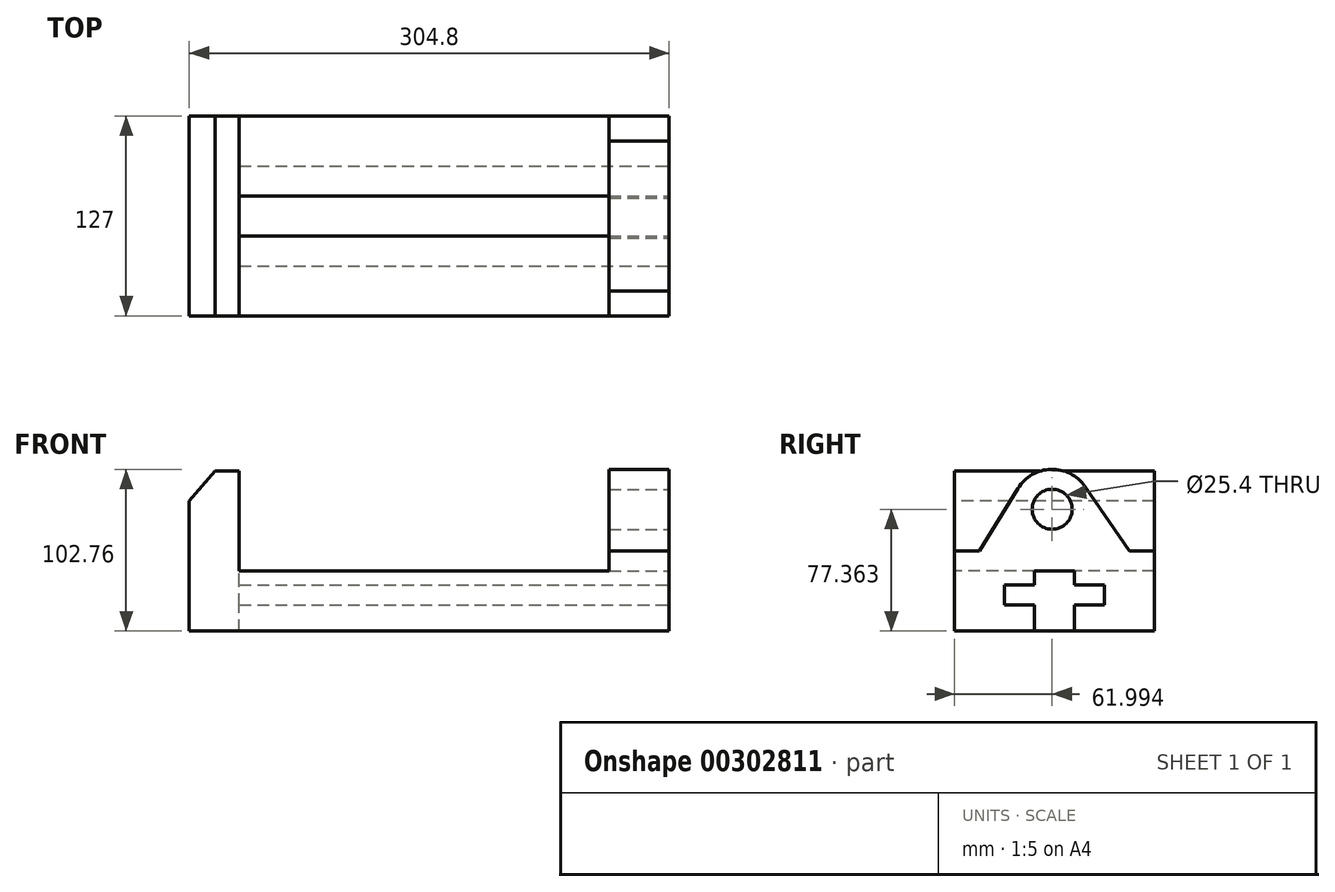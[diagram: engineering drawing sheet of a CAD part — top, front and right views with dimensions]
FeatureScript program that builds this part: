
annotation { "Feature Type Name" : "Feature", "Feature Type Description" : "" }
export const myFeature = defineFeature(function(context is Context, id is Id, definition is map)
    precondition{}
    {
        {
            var Q0;
            Q0=qCreatedBy(makeId("Front.planeOp"),FACE);
            var sketch = newSketch(context, id + "F0", { "sketchPlane" : qUnion([Q0])});
            skLineSegment(sketch, "E0", {"start": v(0, 0) * mm, "end": v(0, 38.1) * mm});
            skLineSegment(sketch, "E1", {"start": v(0, 38.1) * mm, "end": v(304.8, 38.1) * mm});
            skLineSegment(sketch, "E2", {"start": v(0, 0) * mm, "end": v(304.8, 0) * mm});
            skLineSegment(sketch, "E3", {"start": v(304.8, 0) * mm, "end": v(304.8, 38.1) * mm});
            skSolve(sketch);
        }
        {
            var Q0;
            Q0 = qSketchRegion(id + "F0", true);
            extrude(context, id + "F1", {"entities" : qUnion([Q0]), "endBound" : BoundingType.SYMMETRIC, "depth" : 127 * mm});
        }
        {
            var Q0;
            Q0=makeQuery(id+"F1.opExtrude","CAP_FACE",FACE,{"disambiguationData":[OSD([sQuery(id+"F0.wireOp",EDGE,"E0"),sQuery(id+"F0.wireOp",EDGE,"E1"),sQuery(id+"F0.wireOp",EDGE,"E2"),sQuery(id+"F0.wireOp",EDGE,"E3")])],"isStart":false});
            var sketch = newSketch(context, id + "F2", { "sketchPlane" : qUnion([Q0])});
            skLineSegment(sketch, "E4", {"start": v(0, 38.1) * mm, "end": v(31.75, 38.1) * mm});
            skLineSegment(sketch, "E5", {"start": v(31.75, 38.1) * mm, "end": v(31.75, 101.6) * mm});
            skLineSegment(sketch, "E6", {"start": v(0, 38.1) * mm, "end": v(0, 82.55) * mm});
            skLineSegment(sketch, "E7", {"start": v(31.75, 101.6) * mm, "end": v(16.5, 101.6) * mm});
            skLineSegment(sketch, "E8", {"start": v(16.5, 101.6) * mm, "end": v(0, 82.55) * mm});
            skSolve(sketch);
        }
        {
            var Q0;
            Q0 = qSketchRegion(id + "F2", true);
            extrude(context, id + "F3", {"entities" : qUnion([Q0]), "operationType" : NewBodyOperationType.ADD, "oppositeDirection" : true, "depth" : 127 * mm});
        }
        {
            var Q0;
            Q0=makeQuery(id+"F1.opExtrude","SWEPT_FACE",FACE,{"disambiguationData":[OSD([sQuery(id+"F0.wireOp",EDGE,"E3")])]});
            var sketch = newSketch(context, id + "F4", { "sketchPlane" : qUnion([Q0])});
            skLineSegment(sketch, "E9", {"start": v(-63.5, 0) * mm, "end": v(-63.5, 50.8) * mm});
            skLineSegment(sketch, "E10", {"start": v(-63.5, 0) * mm, "end": v(63.5, 0) * mm});
            skLineSegment(sketch, "E11", {"start": v(63.5, 0) * mm, "end": v(63.5, 50.8) * mm});
            skLineSegment(sketch, "E12", {"start": v(-63.5, 50.8) * mm, "end": v(-47.62, 50.8) * mm});
            skLineSegment(sketch, "E13", {"start": v(63.5, 50.8) * mm, "end": v(47.62, 50.8) * mm});
            skLineSegment(sketch, "E14", {"start": v(-47.62, 50.8) * mm, "end": v(-23.15, 90.65) * mm});
            skLineSegment(sketch, "E15", {"start": v(47.62, 50.8) * mm, "end": v(19.41, 91.77) * mm});
            skArc(sketch, "E16", {"start": v(19.41, 91.77) * mm, "mid": v(-2.17, 102.75) * mm, "end": v(-23.15, 90.65) * mm});
            skSolve(sketch);
        }
        {
            var Q0;
            Q0 = qSketchRegion(id + "F4", true);
            extrude(context, id + "F5", {"entities" : qUnion([Q0]), "operationType" : NewBodyOperationType.ADD, "oppositeDirection" : true, "depth" : 38.1 * mm});
        }
        {
            var Q0;
            Q0=makeQuery(id+"F5.boolean.opBoolean","MERGE",FACE,{"derivedFrom":[makeQuery(id+"F1.opExtrude","SWEPT_FACE",FACE,{"disambiguationData":[OSD([sQuery(id+"F0.wireOp",EDGE,"E3")])]}),makeQuery(id+"F5.opExtrude","CAP_FACE",FACE,{"disambiguationData":[OSD([sQuery(id+"F4.wireOp",EDGE,"E9"),sQuery(id+"F4.wireOp",EDGE,"E10"),sQuery(id+"F4.wireOp",EDGE,"E11"),sQuery(id+"F4.wireOp",EDGE,"E12"),sQuery(id+"F4.wireOp",EDGE,"E13"),sQuery(id+"F4.wireOp",EDGE,"E14"),sQuery(id+"F4.wireOp",EDGE,"E15"),sQuery(id+"F4.wireOp",EDGE,"E16")])],"isStart":true})]});
            var sketch = newSketch(context, id + "F6", { "sketchPlane" : qUnion([Q0])});
            skCircle(sketch, "E17", {"center": v(-1.5, 77.36) * mm, "radius": 12.7 * mm});
            skSolve(sketch);
        }
        {
            var Q0;
            Q0 = qSketchRegion(id + "F6", true);
            extrude(context, id + "F7", {"entities" : qUnion([Q0]), "operationType" : NewBodyOperationType.REMOVE, "oppositeDirection" : true, "depth" : 55.88 * mm});
        }
        {
            var Q0;
            Q0=makeQuery(id+"F5.boolean.opBoolean","MERGE",FACE,{"derivedFrom":[makeQuery(id+"F1.opExtrude","SWEPT_FACE",FACE,{"disambiguationData":[OSD([sQuery(id+"F0.wireOp",EDGE,"E3")])]}),makeQuery(id+"F5.opExtrude","CAP_FACE",FACE,{"disambiguationData":[OSD([sQuery(id+"F4.wireOp",EDGE,"E9"),sQuery(id+"F4.wireOp",EDGE,"E10"),sQuery(id+"F4.wireOp",EDGE,"E11"),sQuery(id+"F4.wireOp",EDGE,"E12"),sQuery(id+"F4.wireOp",EDGE,"E13"),sQuery(id+"F4.wireOp",EDGE,"E14"),sQuery(id+"F4.wireOp",EDGE,"E15"),sQuery(id+"F4.wireOp",EDGE,"E16")])],"isStart":true})]});
            var sketch = newSketch(context, id + "F8", { "sketchPlane" : qUnion([Q0])});
            skLineSegment(sketch, "E18", {"start": v(0, 0) * mm, "end": v(-12.7, 0) * mm});
            skLineSegment(sketch, "E19", {"start": v(0, 0) * mm, "end": v(12.7, 0) * mm});
            skLineSegment(sketch, "E20", {"start": v(-12.7, 0) * mm, "end": v(-12.7, 16.51) * mm});
            skLineSegment(sketch, "E21", {"start": v(-12.7, 16.51) * mm, "end": v(-31.75, 16.51) * mm});
            skLineSegment(sketch, "E22", {"start": v(-31.75, 16.51) * mm, "end": v(-31.75, 29.21) * mm});
            skLineSegment(sketch, "E23", {"start": v(-31.75, 29.21) * mm, "end": v(-12.7, 29.21) * mm});
            skLineSegment(sketch, "E24", {"start": v(-12.7, 29.21) * mm, "end": v(-12.7, 38.1) * mm});
            skLineSegment(sketch, "E25", {"start": v(-12.7, 38.1) * mm, "end": v(12.7, 38.1) * mm});
            skLineSegment(sketch, "E26", {"start": v(12.7, 38.1) * mm, "end": v(12.7, 29.21) * mm});
            skLineSegment(sketch, "E27", {"start": v(12.7, 29.21) * mm, "end": v(31.75, 29.21) * mm});
            skLineSegment(sketch, "E28", {"start": v(31.75, 29.21) * mm, "end": v(31.75, 16.51) * mm});
            skLineSegment(sketch, "E29", {"start": v(31.75, 16.51) * mm, "end": v(12.7, 16.51) * mm});
            skLineSegment(sketch, "E30", {"start": v(12.7, 16.51) * mm, "end": v(12.7, 0) * mm});
            skSolve(sketch);
        }
        {
            var Q0;
            Q0 = qSketchRegion(id + "F8", true);
            extrude(context, id + "F9", {"entities" : qUnion([Q0]), "operationType" : NewBodyOperationType.REMOVE, "oppositeDirection" : true, "depth" : 273.05 * mm});
        }
    });
